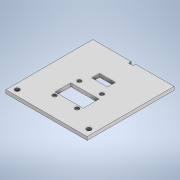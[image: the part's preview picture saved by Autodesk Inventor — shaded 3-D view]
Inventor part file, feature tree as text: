
AUTODESK INVENTOR PART (.ipt)
format: ipt  version: 2021 (Build 250183000, 183)  size: 190,976 bytes
history: native  units: mm
features: thread x6, extrude x3, other x1, sketch x1
ambient origin geometry x8: Origin, YZ Plane, XZ Plane, XY Plane, X Axis, Y Axis, Z Axis, Center Point
bodies: Body1 (feature_tree)
feature tree (11):
  other  "Sólido1"
  sketch  "Boceto1"  dims[d0=36.0mm d1=0.0mm d2=77.0mm d3=0.0mm d4=72.0mm d5=5.0mm d6=5.0mm d7=1.5mm d8=5.0mm d9=5.0mm d10=4.0mm d11=4.0mm d12=3.0mm d13=0.0mm d14=36.0mm d15=2.25mm d16=2.0mm d17=2.0mm d18=50.0mm d19=25.0mm d20=14.0mm d21=5.4mm d22=2.5mm d23=2.5mm d24=2.5mm d25=2.5mm d26=3.5mm d27=3.5mm d28=27.0mm d29=25.0mm d30=2.5mm d31=2.5mm d32=2.5mm d33=2.5mm d34=3.5mm d35=3.5mm d36=1.5mm d37=0.0mm d38=3.0mm d39=0.0mm d40=3.0mm d41=0.0mm d42=1.5mm d43=0.0mm d44=1.5mm d45=0.0mm d46=1.5mm d47=0.0mm d48=1.5mm d49=0.0mm d50=8.0mm d51=8.0mm d52=1.0mm d53=0.0mm d61=30.0mm d63=7.0mm d64=14.0mm d65=7.0mm d66=0.0mm]
  extrude  "Extrusión1"  TaperAngle=0.0deg  [1 undecoded]
  extrude  "Extrusión2"  Depth=77.0mm
  thread  "Rosca1"  [1 undecoded]
  thread  "Rosca2"  [1 undecoded]
  thread  "Rosca3"  [1 undecoded]
  thread  "Rosca4"  [1 undecoded]
  thread  "Rosca5"  [1 undecoded]
  thread  "Rosca6"  [1 undecoded]
  extrude  "Extrusión3"  Depth=5.0mm
note: 7 required parameter values undecoded (feature->parameter linkage not recoverable at this tier; creation-order binding heuristic only, values carry confidence <= 0.55)
